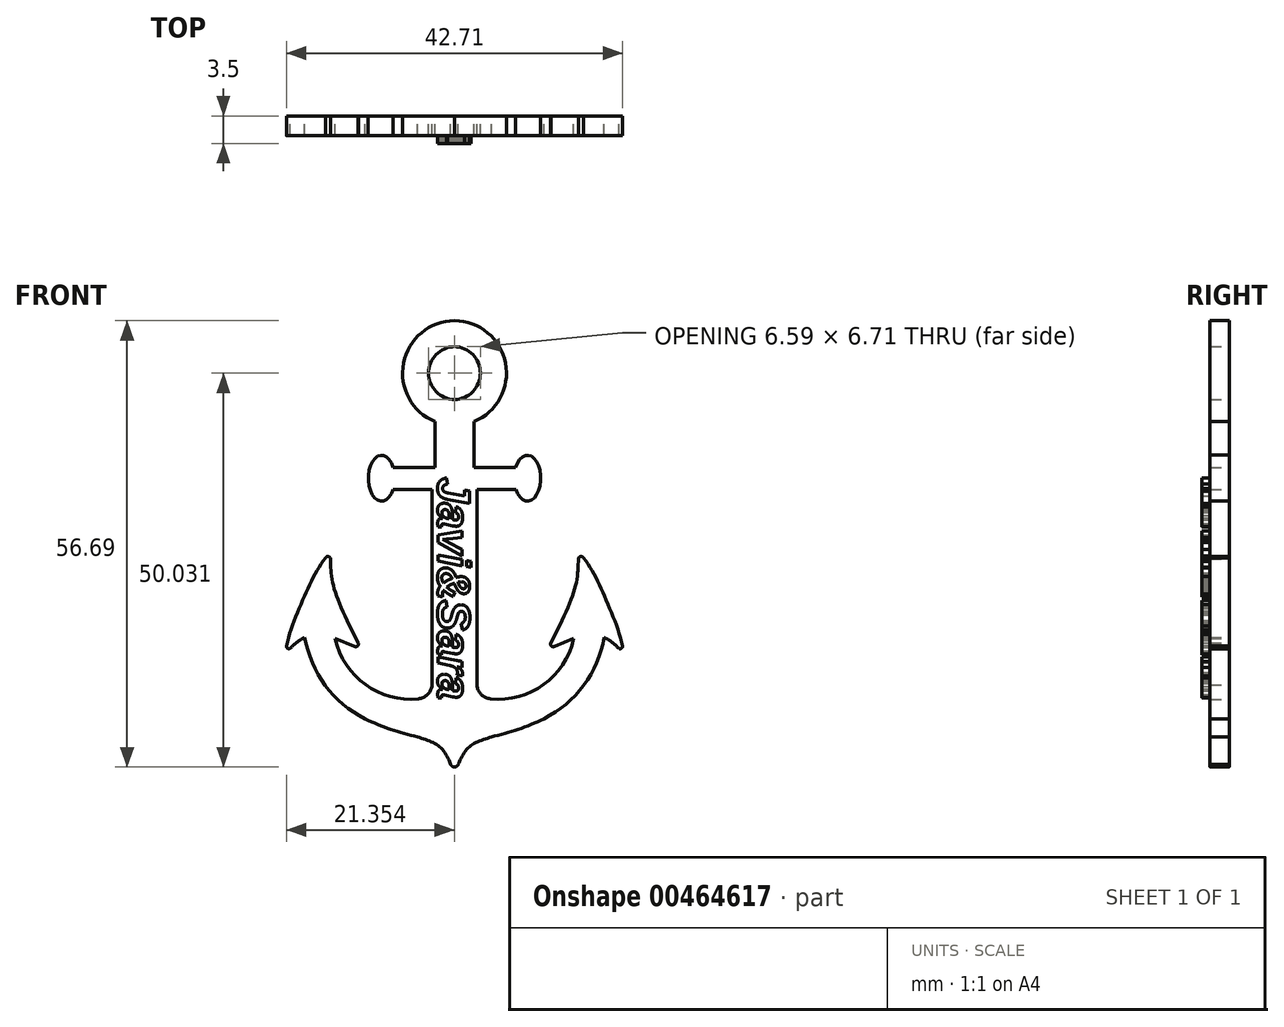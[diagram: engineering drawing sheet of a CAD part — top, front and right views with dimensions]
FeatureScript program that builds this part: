
annotation { "Feature Type Name" : "Feature", "Feature Type Description" : "" }
export const myFeature = defineFeature(function(context is Context, id is Id, definition is map)
    precondition{}
    {
        {
            var Q0;
            Q0=qCreatedBy(makeId("Front.planeOp"),FACE);
            var sketch = newSketch(context, id + "F0", { "sketchPlane" : qUnion([Q0])});
            skLineSegment(sketch, "E0", {"start": v(17.5, 38.25) * mm, "end": v(17.5, -15.99) * mm, "construction": true});
            skLineSegment(sketch, "E1", {"start": v(17.5, 38.25) * mm, "end": v(17.5, 50.76) * mm, "construction": true});
            skArc(sketch, "E2", {"start": v(17.5, 41.58) * mm, "mid": v(14.21, 38.22) * mm, "end": v(17.5, 34.86) * mm});
            skArc(sketch, "E3", {"start": v(17.5, 44.88) * mm, "mid": v(11.03, 39.48) * mm, "end": v(15.04, 32.06) * mm});
            skLineSegment(sketch, "E4", {"start": v(15.04, 32.06) * mm, "end": v(15.04, 26.25) * mm});
            skLineSegment(sketch, "E5", {"start": v(9.74, 26.25) * mm, "end": v(15.04, 26.25) * mm});
            skLineSegment(sketch, "E6", {"start": v(9.72, 23.44) * mm, "end": v(14.65, 23.44) * mm});
            skLineSegment(sketch, "E7", {"start": v(14.65, 23.44) * mm, "end": v(14.65, -1.41) * mm});
            skPoint(sketch, "E8.1.internal.orphan", {"position": v(14.65, -2.72) * mm});
            skPoint(sketch, "E8.3.internal.orphan", {"position": v(14.67, -1.41) * mm});
            skArc(sketch, "E9", {"start": v(12.92, -3.17) * mm, "mid": v(14.1, -2.6) * mm, "end": v(14.67, -1.41) * mm});
            skArc(sketch, "E10", {"start": v(2.36, 4.48) * mm, "mid": v(6.18, -1.35) * mm, "end": v(12.92, -3.17) * mm});
            skLineSegment(sketch, "E11", {"start": v(2.36, 4.48) * mm, "end": v(4.83, 3.48) * mm});
            skArc(sketch, "E12", {"start": v(4.83, 3.48) * mm, "mid": v(5.2, 3.57) * mm, "end": v(5.27, 3.95) * mm});
            skArc(sketch, "E13", {"start": v(1.78, 14.63) * mm, "mid": v(1.49, 14.91) * mm, "end": v(1.11, 14.76) * mm});
            skFitSpline(sketch, "E14", {"points": [v(1.11, 14.76) * mm, v(-1.53, 9.92) * mm, v(-3.85, 3.57) * mm], "startDerivative": vector(-7.02, -8.94) * mm, "endDerivative": vector(-2.6, -11.75) * mm});
            skArc(sketch, "E15", {"start": v(-3.85, 3.57) * mm, "mid": v(-3.71, 3.26) * mm, "end": v(-3.38, 3.24) * mm});
            skFitSpline(sketch, "E16", {"points": [v(-3.38, 3.24) * mm, v(-2.47, 4.07) * mm, v(-1.5, 4.64) * mm], "startDerivative": vector(1.73, 1.74) * mm, "endDerivative": vector(2.02, 1.07) * mm});
            skArc(sketch, "E17", {"start": v(-1.5, 4.64) * mm, "mid": v(1.1, -1.44) * mm, "end": v(6.14, -5.7) * mm});
            skArc(sketch, "E18", {"start": v(6.14, -5.7) * mm, "mid": v(9.41, -7.05) * mm, "end": v(12.82, -8) * mm});
            skFitSpline(sketch, "E19", {"points": [v(12.82, -8) * mm, v(14.03, -8.4) * mm, v(15.12, -8.9) * mm, v(15.98, -9.61) * mm, v(16.68, -10.72) * mm, v(17.03, -11.5) * mm], "startDerivative": vector(5.78, -1.86) * mm, "endDerivative": vector(1.73, -4.28) * mm});
            skArc(sketch, "E20", {"start": v(17.03, -11.5) * mm, "mid": v(17.21, -11.73) * mm, "end": v(17.5, -11.8) * mm});
            skEllipticalArc(sketch, "E21", {});
            skLineSegment(sketch, "E22", {"start": v(9.74, 26.25) * mm, "end": v(9.73, 26.25) * mm});
            skArc(sketch, "E23.MirrorCS", {"start": v(17.5, 44.88) * mm, "mid": v(23.98, 39.48) * mm, "end": v(19.97, 32.06) * mm});
            skArc(sketch, "E24.MirrorCS", {"start": v(17.5, 41.58) * mm, "mid": v(20.8, 38.22) * mm, "end": v(17.5, 34.86) * mm});
            skLineSegment(sketch, "E25.MirrorCS", {"start": v(19.97, 32.06) * mm, "end": v(19.97, 26.25) * mm});
            skLineSegment(sketch, "E26.MirrorCS", {"start": v(25.27, 26.25) * mm, "end": v(19.97, 26.25) * mm});
            skEllipticalArc(sketch, "E27.MirrorCS", {});
            skLineSegment(sketch, "E28.MirrorCS", {"start": v(25.3, 23.44) * mm, "end": v(20.36, 23.44) * mm});
            skLineSegment(sketch, "E29.MirrorCS", {"start": v(20.36, 23.44) * mm, "end": v(20.36, -1.41) * mm});
            skArc(sketch, "E30.MirrorCS", {"start": v(22.1, -3.17) * mm, "mid": v(20.9, -2.6) * mm, "end": v(20.34, -1.41) * mm});
            skArc(sketch, "E31.MirrorCS", {"start": v(32.64, 4.48) * mm, "mid": v(28.82, -1.35) * mm, "end": v(22.1, -3.17) * mm});
            skLineSegment(sketch, "E32.MirrorCS", {"start": v(32.64, 4.48) * mm, "end": v(30.18, 3.48) * mm});
            skArc(sketch, "E33.MirrorCS", {"start": v(30.18, 3.48) * mm, "mid": v(29.8, 3.57) * mm, "end": v(29.73, 3.95) * mm});
            skArc(sketch, "E34.MirrorCS", {"start": v(33.23, 14.63) * mm, "mid": v(33.52, 14.91) * mm, "end": v(33.9, 14.76) * mm});
            skFitSpline(sketch, "E35.MirrorCS", {"points": [v(33.9, 14.76) * mm, v(36.54, 9.92) * mm, v(38.86, 3.57) * mm], "startDerivative": vector(7.02, -8.94) * mm, "endDerivative": vector(2.6, -11.75) * mm});
            skArc(sketch, "E36.MirrorCS", {"start": v(38.86, 3.57) * mm, "mid": v(38.72, 3.26) * mm, "end": v(38.39, 3.24) * mm});
            skFitSpline(sketch, "E37.MirrorCS", {"points": [v(38.39, 3.24) * mm, v(37.48, 4.07) * mm, v(36.51, 4.64) * mm], "startDerivative": vector(-1.73, 1.74) * mm, "endDerivative": vector(-2.02, 1.07) * mm});
            skArc(sketch, "E38.MirrorCS", {"start": v(36.51, 4.64) * mm, "mid": v(33.91, -1.44) * mm, "end": v(28.86, -5.7) * mm});
            skFitSpline(sketch, "E39.MirrorCS", {"points": [v(22.19, -8) * mm, v(20.97, -8.4) * mm, v(19.89, -8.9) * mm, v(19.03, -9.61) * mm, v(18.32, -10.72) * mm, v(17.98, -11.5) * mm], "startDerivative": vector(-5.78, -1.86) * mm, "endDerivative": vector(-1.73, -4.28) * mm});
            skArc(sketch, "E40.MirrorCS", {"start": v(17.98, -11.5) * mm, "mid": v(17.8, -11.73) * mm, "end": v(17.5, -11.8) * mm});
            skArc(sketch, "E41.MirrorCS", {"start": v(28.86, -5.7) * mm, "mid": v(25.6, -7.05) * mm, "end": v(22.19, -8) * mm});
            skPoint(sketch, "E42.orphan", {"position": v(17.5, 31.56) * mm});
            skLineSegment(sketch, "E43", {"start": v(25.27, 26.25) * mm, "end": v(25.28, 26.25) * mm});
            skFitSpline(sketch, "E44", {"points": [v(5.27, 3.95) * mm, v(2.73, 9.36) * mm, v(1.89, 12.43) * mm, v(1.78, 14.63) * mm], "startDerivative": vector(-6.76, 13.38) * mm, "endDerivative": vector(-0.06, 8.28) * mm});
            skFitSpline(sketch, "E45.MirrorCS", {"points": [v(29.73, 3.95) * mm, v(32.28, 9.36) * mm, v(33.12, 12.43) * mm, v(33.23, 14.63) * mm], "startDerivative": vector(6.76, 13.38) * mm, "endDerivative": vector(0.06, 8.28) * mm});
            skLineSegment(sketch, "E46", {"start": v(15.04, 32.06) * mm, "end": v(19.97, 32.06) * mm});
            skLineSegment(sketch, "E47", {"start": v(9.72, 23.44) * mm, "end": v(9.74, 26.25) * mm});
            skLineSegment(sketch, "E48", {"start": v(25.3, 23.44) * mm, "end": v(25.28, 26.25) * mm});
            skLineSegment(sketch, "E49", {"start": v(32.64, 4.48) * mm, "end": v(36.51, 4.64) * mm});
            skLineSegment(sketch, "E50", {"start": v(14.67, -1.41) * mm, "end": v(20.36, -1.41) * mm});
            skLineSegment(sketch, "E51", {"start": v(-1.5, 4.64) * mm, "end": v(2.36, 4.48) * mm});
            skLineSegment(sketch, "E52", {"start": v(20.34, -1.41) * mm, "end": v(20.36, -1.41) * mm});
            skLineSegment(sketch, "E53", {"start": v(14.65, -1.41) * mm, "end": v(14.67, -1.41) * mm});
            const initialGuessF0  = {"E21": [0.008244960568845272, 0.024870822206139565, 0, 1, 0.0029189549386501312, 0.0016869629892020657, 5.206327264973328, 4.201301801492759], "E27.MirrorCS": [0.02676210645586252, 0.024870822206139568, 0, 1, 0.0029189549386501312, 0.0016869629892020657, 2.081883505686827, 1.0768580422062581]};
            skSetInitialGuess(sketch, initialGuessF0);
            skSolve(sketch);
        }
        {
            var Q0;
            Q0=makeQuery(id+"F0.imprint","IMPRINT",FACE,{"disambiguationData":[TD([[makeQuery(id+"F0.imprint","IMPRINT",EDGE,{"derivedFrom":sQuery(id+"F0.wireOp",EDGE,"E4")}),1.0]])]});
            var Q1;
            Q1=makeQuery(id+"F0.imprint","IMPRINT",FACE,{"disambiguationData":[TD([[makeQuery(id+"F0.imprint","IMPRINT",EDGE,{"derivedFrom":sQuery(id+"F0.wireOp",EDGE,"E27.MirrorCS")}),1.0]])]});
            var Q2;
            Q2=makeQuery(id+"F0.imprint","IMPRINT",FACE,{"disambiguationData":[TD([[makeQuery(id+"F0.imprint","IMPRINT",EDGE,{"derivedFrom":sQuery(id+"F0.wireOp",EDGE,"E2")}),-1.0]])]});
            var Q3;
            Q3=makeQuery(id+"F0.imprint","IMPRINT",FACE,{"disambiguationData":[TD([[makeQuery(id+"F0.imprint","IMPRINT",EDGE,{"derivedFrom":sQuery(id+"F0.wireOp",EDGE,"E21")}),1.0]])]});
            var Q4;
            Q4=makeQuery(id+"F0.imprint","IMPRINT",FACE,{"disambiguationData":[TD([[makeQuery(id+"F0.imprint","IMPRINT",EDGE,{"derivedFrom":sQuery(id+"F0.wireOp",EDGE,"E9")}),-1.0]])]});
            var Q5;
            Q5=makeQuery(id+"F0.imprint","IMPRINT",FACE,{"disambiguationData":[TD([[makeQuery(id+"F0.imprint","IMPRINT",EDGE,{"derivedFrom":sQuery(id+"F0.wireOp",EDGE,"E11")}),1.0]])]});
            var Q6;
            Q6=makeQuery(id+"F0.imprint","IMPRINT",FACE,{"disambiguationData":[TD([[makeQuery(id+"F0.imprint","IMPRINT",EDGE,{"derivedFrom":sQuery(id+"F0.wireOp",EDGE,"E32.MirrorCS")}),-1.0]])]});
            extrude(context, id + "F1", {"entities" : qUnion([Q0, Q1, Q2, Q3, Q4, Q5, Q6]), "depth" : 2.5 * mm});
        }
        {
            var Q0;
            Q0=makeQuery(id+"F1.opExtrude","CAP_FACE",FACE,{"disambiguationData":[OSD([sQuery(id+"F0.wireOp",EDGE,"E2"),sQuery(id+"F0.wireOp",EDGE,"E3"),sQuery(id+"F0.wireOp",EDGE,"E4"),sQuery(id+"F0.wireOp",EDGE,"E5"),sQuery(id+"F0.wireOp",EDGE,"E6"),sQuery(id+"F0.wireOp",EDGE,"E7"),sQuery(id+"F0.wireOp",EDGE,"E9"),sQuery(id+"F0.wireOp",EDGE,"E10"),sQuery(id+"F0.wireOp",EDGE,"E11"),sQuery(id+"F0.wireOp",EDGE,"E12"),sQuery(id+"F0.wireOp",EDGE,"E13"),sQuery(id+"F0.wireOp",EDGE,"E14"),sQuery(id+"F0.wireOp",EDGE,"E15"),sQuery(id+"F0.wireOp",EDGE,"E16"),sQuery(id+"F0.wireOp",EDGE,"E17"),sQuery(id+"F0.wireOp",EDGE,"E18"),sQuery(id+"F0.wireOp",EDGE,"E19"),sQuery(id+"F0.wireOp",EDGE,"E20"),sQuery(id+"F0.wireOp",EDGE,"E21"),sQuery(id+"F0.wireOp",EDGE,"E22"),sQuery(id+"F0.wireOp",EDGE,"E23.MirrorCS"),sQuery(id+"F0.wireOp",EDGE,"E24.MirrorCS"),sQuery(id+"F0.wireOp",EDGE,"E25.MirrorCS"),sQuery(id+"F0.wireOp",EDGE,"E26.MirrorCS"),sQuery(id+"F0.wireOp",EDGE,"E27.MirrorCS"),sQuery(id+"F0.wireOp",EDGE,"E28.MirrorCS"),sQuery(id+"F0.wireOp",EDGE,"E29.MirrorCS"),sQuery(id+"F0.wireOp",EDGE,"E30.MirrorCS"),sQuery(id+"F0.wireOp",EDGE,"E31.MirrorCS"),sQuery(id+"F0.wireOp",EDGE,"E32.MirrorCS"),sQuery(id+"F0.wireOp",EDGE,"E33.MirrorCS"),sQuery(id+"F0.wireOp",EDGE,"E34.MirrorCS"),sQuery(id+"F0.wireOp",EDGE,"E35.MirrorCS"),sQuery(id+"F0.wireOp",EDGE,"E36.MirrorCS"),sQuery(id+"F0.wireOp",EDGE,"E37.MirrorCS"),sQuery(id+"F0.wireOp",EDGE,"E38.MirrorCS"),sQuery(id+"F0.wireOp",EDGE,"E39.MirrorCS"),sQuery(id+"F0.wireOp",EDGE,"E40.MirrorCS"),sQuery(id+"F0.wireOp",EDGE,"E41.MirrorCS"),sQuery(id+"F0.wireOp",EDGE,"E43"),sQuery(id+"F0.wireOp",EDGE,"E44"),sQuery(id+"F0.wireOp",EDGE,"E45.MirrorCS"),sQuery(id+"F0.wireOp",EDGE,"E52"),sQuery(id+"F0.wireOp",EDGE,"E53")])],"isStart":false});
            var sketch = newSketch(context, id + "F2", { "sketchPlane" : qUnion([Q0])});
            skText(sketch, "E54", { "text": "Javi&Sara", "fontName": "Arimo-BoldItalic.ttf"});
            const initialGuessF2  = {"E54": [0.0154, 0.02497, 0, -1, 0.0042]};
            skSetInitialGuess(sketch, initialGuessF2);
            skSolve(sketch);
        }
        {
            var Q0;
            Q0 = qSketchRegion(id + "F2", true);
            extrude(context, id + "F3", {"entities" : qUnion([Q0]), "operationType" : NewBodyOperationType.ADD, "depth" : 1 * mm});
        }
    });
